# Revit family: Konsole 45- 52 D Platte längs
name_source: partatom
category: HLS-Bauteile
revit_build: Autodesk Revit 2017 (Build: 20190507_1515(x64)
units: mm (PartAtom-declared; Revit-internal decimal feet)

## family parameters
Basisbauteil = Fläche
Beim Laden mit Abzugskörper schneiden = Nein
Bemaßung runder Anschluss = Durchmesser verwenden
Gemeinsam genutzt = Ja
Raumberechnungspunkt = Nein
Teiletyp = Normal

## types (4) — shared parameters
Ausrichtung Platte = längs
Breite Platte = 50 mm  [stored 0.164042 ft]
Breite Profil = 45 mm  [stored 0.147638 ft]
Fabrikat = MEFA
Firma = MEFA Befestigungs- und Montagesysteme GmbH
Höhe Profil = 52 mm
Kurztext1 = Konsole C-Profil 45/52
Langloch Platte = 14x20 mm
Lochabstand = 87 mm
Länge Platte = 130 mm  [stored 0.426509 ft]
Material = Stahl
Materialname C-Profil = S235JR
Materialname Platte = S235JR
Oberflaeche = galvanisch verzinkt
Profil = Doppel-C-Profil
Stärke Platte = 8 mm  [stored 0.0262467 ft]
Stärke Profil = 2 mm  [stored 0.00656168 ft]
Vorgabe-Ansicht = 1219 mm

## per-type parameters (varying)
| type | Artikelnummer | EAN | Gewicht | Gewicht pro Bauteil | Kurztext2 | Länge Konsole | Schienenlänge | max. zul. Last F1 | max. zul. Last F2 | max. zul. Last q0 |
| Konsole 45- 52 D L= 630 Platte längs gvz | 18070630 | 4250928437785 | 2.06 kg | 2.06 kg | L= 630 mm Platte längs gvz | 630 mm  [stored 2.06693 ft] | Montageschiene 45- 52-1,5 D für Konsole : C-Profil 45- 52-1,5 D L=  630 | 0.33 kip | 0.16 kip | 0.160 kip/ft |
| Konsole 45- 52 D L= 525 Platte längs gvz | 18070525 | 4250928437778 | 1.78 kg | 1.78 kg | L= 525 mm Platte längs gvz | 525 mm | Montageschiene 45- 52-1,5 D für Konsole : C-Profil 45- 52-1,5 D L=  525 | 0.40 kip | 0.20 kip | 0.230 kip/ft |
| Konsole 45- 52 D L= 420 Platte längs gvz | 18070420 | 4250928437761 | 1.50 kg | 1.50 kg | L= 420 mm Platte längs gvz | 420 mm  [stored 1.37795 ft] | Montageschiene 45- 52-1,5 D für Konsole : C-Profil 45- 52-1,5 D L=  420 | 0.49 kip | 0.25 kip | 0.358 kip/ft |
| Konsole 45- 52 D L= 315 Platte längs gvz | 18070315 | 4250928437754 | 1.21 kg | 1.21 kg | L= 315 mm Platte längs gvz | 315 mm  [stored 1.03346 ft] | Montageschiene 45- 52-1,5 D für Konsole : C-Profil 45- 52-1,5 D L=  315 | 0.66 kip | 0.33 kip | 0.637 kip/ft |

note: [stored X ft] marks values corroborated as IEEE doubles in the binary element streams (Revit-internal decimal feet)
